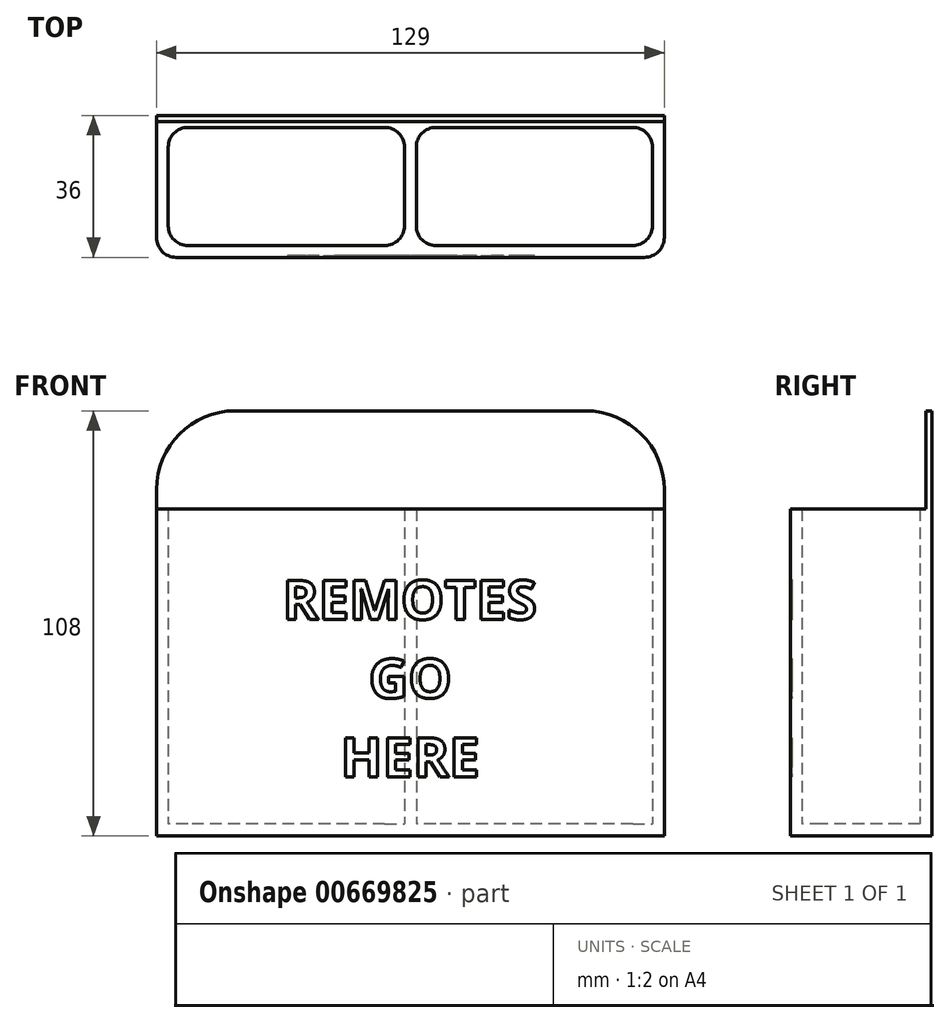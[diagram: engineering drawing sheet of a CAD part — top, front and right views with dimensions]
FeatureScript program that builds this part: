
annotation { "Feature Type Name" : "Feature", "Feature Type Description" : "" }
export const myFeature = defineFeature(function(context is Context, id is Id, definition is map)
    precondition{}
    {
        {
            var Q0;
            Q0=qCreatedBy(makeId("Top.planeOp"),FACE);
            var sketch = newSketch(context, id + "F0", { "sketchPlane" : qUnion([Q0])});
            skLineSegment(sketch, "E0.bottom", {"start": v(64.5, 18) * mm, "end": v(-64.5, 18) * mm});
            skLineSegment(sketch, "E0.top", {"start": v(64.5, -18) * mm, "end": v(-64.5, -18) * mm});
            skLineSegment(sketch, "E0.left", {"start": v(64.5, 18) * mm, "end": v(64.5, -18) * mm});
            skLineSegment(sketch, "E0.right", {"start": v(-64.5, 18) * mm, "end": v(-64.5, -18) * mm});
            skPoint(sketch, "E0.middle", {"position": v(0, 0) * mm});
            skSolve(sketch);
        }
        {
            var Q0;
            Q0=makeQuery(id+"F0.imprint","IMPRINT",FACE,{"disambiguationData":[TD([[makeQuery(id+"F0.imprint","IMPRINT",EDGE,{"derivedFrom":sQuery(id+"F0.wireOp",EDGE,"E0.bottom")}),1.0]])]});
            extrude(context, id + "F1", {"entities" : qUnion([Q0]), "depth" : 3 * mm, "offsetDistance" : 25 * mm});
        }
        {
            var Q0;
            Q0=makeQuery(id+"F1.opExtrude","CAP_FACE",FACE,{"disambiguationData":[OSD([sQuery(id+"F0.wireOp",EDGE,"E0.bottom"),sQuery(id+"F0.wireOp",EDGE,"E0.top"),sQuery(id+"F0.wireOp",EDGE,"E0.left"),sQuery(id+"F0.wireOp",EDGE,"E0.right")])],"isStart":false});
            var sketch = newSketch(context, id + "F2", { "sketchPlane" : qUnion([Q0])});
            skLineSegment(sketch, "E1.0", {"start": v(64.5, 18) * mm, "end": v(-64.5, 18) * mm});
            skLineSegment(sketch, "E2.0", {"start": v(-64.5, 18) * mm, "end": v(-64.5, -18) * mm});
            skLineSegment(sketch, "E3.0", {"start": v(64.5, -18) * mm, "end": v(-64.5, -18) * mm});
            skLineSegment(sketch, "E4.0", {"start": v(64.5, 18) * mm, "end": v(64.5, -18) * mm});
            skLineSegment(sketch, "E5.bottom", {"start": v(61.5, 15) * mm, "end": v(-61.5, 15) * mm});
            skLineSegment(sketch, "E5.top", {"start": v(61.5, -15) * mm, "end": v(-61.5, -15) * mm});
            skLineSegment(sketch, "E5.left", {"start": v(61.5, 15) * mm, "end": v(61.5, -15) * mm});
            skLineSegment(sketch, "E5.right", {"start": v(-61.5, 15) * mm, "end": v(-61.5, -15) * mm});
            skPoint(sketch, "E5.middle", {"position": v(0, 0) * mm});
            skLineSegment(sketch, "E6", {"start": v(1.5, 15) * mm, "end": v(1.5, -15) * mm});
            skLineSegment(sketch, "E7.MirrorCS", {"start": v(-1.5, 15) * mm, "end": v(-1.5, -15) * mm});
            skSolve(sketch);
        }
        {
            var Q0;
            Q0=makeQuery(id+"F2.imprint","IMPRINT",FACE,{"disambiguationData":[TD([[makeQuery(id+"F2.imprint","IMPRINT",EDGE,{"derivedFrom":sQuery(id+"F2.wireOp",EDGE,"E1.0")}),1.0]])]});
            var Q1;
            {var subQ0=sQuery(id+"F2.wireOp",EDGE,"E6");Q1=makeQuery(id+"F2.imprint","IMPRINT",FACE,{"disambiguationData":[TD([[makeQuery(id+"F2.imprint","IMPRINT",EDGE,{"derivedFrom":subQ0}),-1.0]])]});}
            extrude(context, id + "F3", {"entities" : qUnion([Q0, Q1]), "operationType" : NewBodyOperationType.ADD, "depth" : 80 * mm, "offsetDistance" : 25 * mm});
        }
        {
            var Q0;
            Q0=makeQuery(id+"F3.opExtrude","CAP_FACE",FACE,{"disambiguationData":[OSD([sQuery(id+"F2.wireOp",EDGE,"E1.0"),sQuery(id+"F2.wireOp",EDGE,"E2.0"),sQuery(id+"F2.wireOp",EDGE,"E3.0"),sQuery(id+"F2.wireOp",EDGE,"E4.0"),sQuery(id+"F2.wireOp",EDGE,"E5.bottom"),sQuery(id+"F2.wireOp",EDGE,"E5.top"),sQuery(id+"F2.wireOp",EDGE,"E5.left"),sQuery(id+"F2.wireOp",EDGE,"E5.right"),sQuery(id+"F2.wireOp",EDGE,"E6"),sQuery(id+"F2.wireOp",EDGE,"E7.MirrorCS")])],"isStart":false});
            var sketch = newSketch(context, id + "F4", { "sketchPlane" : qUnion([Q0])});
            skLineSegment(sketch, "E8.bottom", {"start": v(-64.5, 18) * mm, "end": v(64.5, 18) * mm});
            skLineSegment(sketch, "E8.top", {"start": v(-64.5, 16.5) * mm, "end": v(64.5, 16.5) * mm});
            skLineSegment(sketch, "E8.left", {"start": v(-64.5, 18) * mm, "end": v(-64.5, 16.5) * mm});
            skLineSegment(sketch, "E8.right", {"start": v(64.5, 18) * mm, "end": v(64.5, 16.5) * mm});
            skSolve(sketch);
        }
        {
            var Q0;
            Q0=makeQuery(id+"F4.imprint","IMPRINT",FACE,{"disambiguationData":[TD([[makeQuery(id+"F4.imprint","IMPRINT",EDGE,{"derivedFrom":sQuery(id+"F4.wireOp",EDGE,"E8.bottom")}),1.0]])]});
            extrude(context, id + "F5", {"entities" : qUnion([Q0]), "operationType" : NewBodyOperationType.ADD, "depth" : 25 * mm, "offsetDistance" : 25 * mm});
        }
        {
            var Q0;
            Q0=makeQuery(id+"F5.opExtrude","CAP_EDGE",EDGE,{"disambiguationData":[OSD([sQuery(id+"F4.wireOp",EDGE,"E8.left")])],"isStart":false});
            var Q1;
            Q1=makeQuery(id+"F5.opExtrude","CAP_EDGE",EDGE,{"disambiguationData":[OSD([sQuery(id+"F4.wireOp",EDGE,"E8.right")])],"isStart":false});
            fillet(context, id + "F6", {"entities" : qUnion([Q0, Q1]), "radius" : 20 * mm, "tangentPropagation" : true, "allowEdgeOverflow" : false});
        }
        {
            var Q0;
            Q0=makeQuery(id+"F3.boolean.opBoolean","MERGE",EDGE,{"derivedFrom":[makeQuery(id+"F1.opExtrude","SWEPT_EDGE",EDGE,{"disambiguationData":[OSD([sQuery(id+"F0.wireOp",EDGE,"E0.top"),sQuery(id+"F0.wireOp",EDGE,"E0.right")])]}),makeQuery(id+"F3.opExtrude","SWEPT_EDGE",EDGE,{"disambiguationData":[OSD([sQuery(id+"F2.wireOp",EDGE,"E2.0"),sQuery(id+"F2.wireOp",EDGE,"E3.0")])]})]});
            var Q1;
            Q1=makeQuery(id+"F3.boolean.opBoolean","MERGE",EDGE,{"derivedFrom":[makeQuery(id+"F1.opExtrude","SWEPT_EDGE",EDGE,{"disambiguationData":[OSD([sQuery(id+"F0.wireOp",EDGE,"E0.top"),sQuery(id+"F0.wireOp",EDGE,"E0.left")])]}),makeQuery(id+"F3.opExtrude","SWEPT_EDGE",EDGE,{"disambiguationData":[OSD([sQuery(id+"F2.wireOp",EDGE,"E3.0"),sQuery(id+"F2.wireOp",EDGE,"E4.0")])]})]});
            fillet(context, id + "F7", {"entities" : qUnion([Q0, Q1]), "radius" : 5 * mm, "tangentPropagation" : true, "allowEdgeOverflow" : false});
        }
        {
            var Q0;
            Q0=makeQuery(id+"F3.opExtrude","SWEPT_EDGE",EDGE,{"disambiguationData":[OSD([sQuery(id+"F2.wireOp",EDGE,"E5.bottom"),sQuery(id+"F2.wireOp",EDGE,"E7.MirrorCS")])]});
            var Q1;
            Q1=makeQuery(id+"F3.opExtrude","SWEPT_EDGE",EDGE,{"disambiguationData":[OSD([sQuery(id+"F2.wireOp",EDGE,"E5.bottom"),sQuery(id+"F2.wireOp",EDGE,"E5.left")])]});
            var Q2;
            Q2=makeQuery(id+"F3.opExtrude","SWEPT_EDGE",EDGE,{"disambiguationData":[OSD([sQuery(id+"F2.wireOp",EDGE,"E5.top"),sQuery(id+"F2.wireOp",EDGE,"E5.left")])]});
            var Q3;
            Q3=makeQuery(id+"F3.opExtrude","SWEPT_EDGE",EDGE,{"disambiguationData":[OSD([sQuery(id+"F2.wireOp",EDGE,"E5.top"),sQuery(id+"F2.wireOp",EDGE,"E7.MirrorCS")])]});
            var Q4;
            Q4=makeQuery(id+"F3.opExtrude","SWEPT_EDGE",EDGE,{"disambiguationData":[OSD([sQuery(id+"F2.wireOp",EDGE,"E5.top"),sQuery(id+"F2.wireOp",EDGE,"E5.right")])]});
            var Q5;
            Q5=makeQuery(id+"F3.opExtrude","SWEPT_EDGE",EDGE,{"disambiguationData":[OSD([sQuery(id+"F2.wireOp",EDGE,"E5.top"),sQuery(id+"F2.wireOp",EDGE,"E6")])]});
            var Q6;
            Q6=makeQuery(id+"F3.opExtrude","SWEPT_EDGE",EDGE,{"disambiguationData":[OSD([sQuery(id+"F2.wireOp",EDGE,"E5.bottom"),sQuery(id+"F2.wireOp",EDGE,"E5.right")])]});
            var Q7;
            Q7=makeQuery(id+"F3.opExtrude","SWEPT_EDGE",EDGE,{"disambiguationData":[OSD([sQuery(id+"F2.wireOp",EDGE,"E5.bottom"),sQuery(id+"F2.wireOp",EDGE,"E6")])]});
            fillet(context, id + "F8", {"entities" : qUnion([Q0, Q1, Q2, Q3, Q4, Q5, Q6, Q7]), "radius" : 5 * mm, "tangentPropagation" : true, "allowEdgeOverflow" : false});
        }
        {
            var Q0;
            Q0=makeQuery(id+"F3.boolean.opBoolean","MERGE",FACE,{"derivedFrom":[makeQuery(id+"F1.opExtrude","SWEPT_FACE",FACE,{"disambiguationData":[OSD([sQuery(id+"F0.wireOp",EDGE,"E0.top")])]}),makeQuery(id+"F3.opExtrude","SWEPT_FACE",FACE,{"disambiguationData":[OSD([sQuery(id+"F2.wireOp",EDGE,"E3.0")])]})]});
            var sketch = newSketch(context, id + "F9", { "sketchPlane" : qUnion([Q0])});
            skText(sketch, "E9", { "text": "REMOTES", "fontName": "OpenSans-Bold.ttf"});
            skText(sketch, "E10", { "text": "GO", "fontName": "OpenSans-Bold.ttf"});
            skText(sketch, "E11", { "text": "HERE", "fontName": "OpenSans-Bold.ttf"});
            const initialGuessF9  = {"E9": [-0.03246, 0.055, 1, 0, 0.01], "E10": [-0.0106, 0.035, 1, 0, 0.01], "E11": [-0.01772, 0.015, 1, 0, 0.01]};
            skSetInitialGuess(sketch, initialGuessF9);
            skSolve(sketch);
        }
        {
            var Q0;
            Q0 = qSketchRegion(id + "F9", true);
            extrude(context, id + "F10", {"entities" : qUnion([Q0]), "operationType" : NewBodyOperationType.REMOVE, "oppositeDirection" : true, "depth" : .5 * mm, "offsetDistance" : 25 * mm, "hasDraft" : true, "draftAngle" : 3 * degree});
        }
    });
